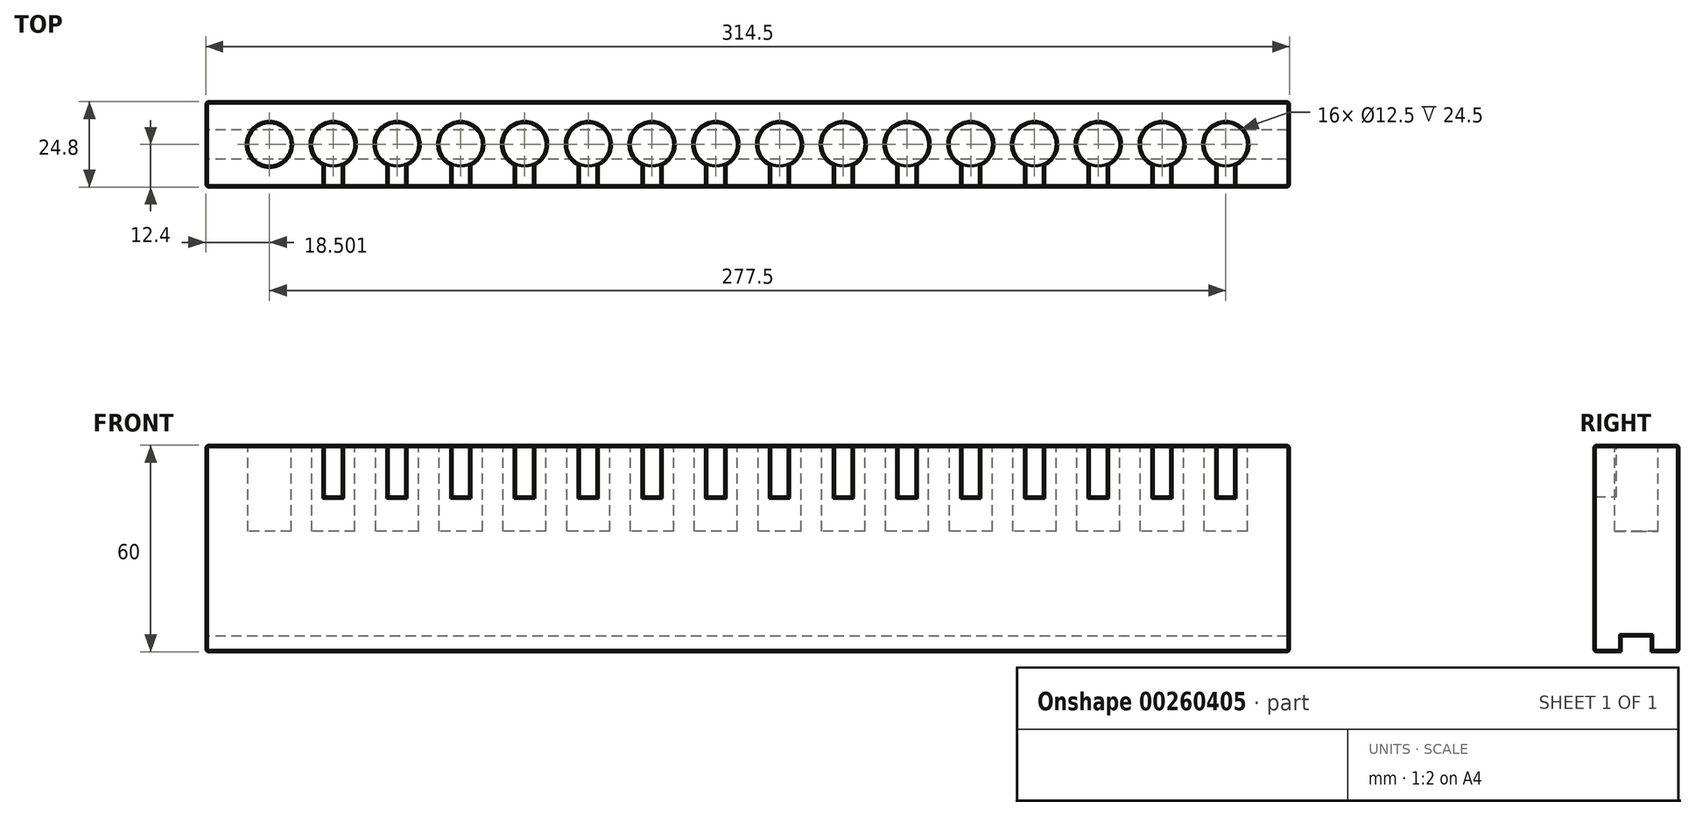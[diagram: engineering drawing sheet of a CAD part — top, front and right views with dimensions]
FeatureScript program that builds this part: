
annotation { "Feature Type Name" : "Feature", "Feature Type Description" : "" }
export const myFeature = defineFeature(function(context is Context, id is Id, definition is map)
    precondition{}
    {
        {
            var Q0;
            Q0=qCreatedBy(makeId("Front.planeOp"),FACE);
            var sketch = newSketch(context, id + "F0", { "sketchPlane" : qUnion([Q0])});
            skLineSegment(sketch, "E0.bottom", {"start": v(-141.6, 0) * mm, "end": v(172.9, 0) * mm});
            skLineSegment(sketch, "E0.top", {"start": v(-141.6, 60) * mm, "end": v(172.9, 60) * mm});
            skLineSegment(sketch, "E0.left", {"start": v(-141.6, 0) * mm, "end": v(-141.6, 60) * mm});
            skLineSegment(sketch, "E0.right", {"start": v(172.9, 0) * mm, "end": v(172.9, 60) * mm});
            skLineSegment(sketch, "E1.bottom", {"start": v(-125.6, 60) * mm, "end": v(-120.6, 60) * mm});
            skLineSegment(sketch, "E1.top", {"start": v(-125.6, 45) * mm, "end": v(-120.6, 45) * mm});
            skLineSegment(sketch, "E1.left", {"start": v(-125.6, 60) * mm, "end": v(-125.6, 45) * mm});
            skLineSegment(sketch, "E1.right", {"start": v(-120.6, 60) * mm, "end": v(-120.6, 45) * mm});
            skLineSegment(sketch, "E2.1.0.0", {"start": v(-107.1, 60) * mm, "end": v(-107.1, 45) * mm});
            skLineSegment(sketch, "E2.1.0.1", {"start": v(-107.1, 60) * mm, "end": v(-102.1, 60) * mm});
            skLineSegment(sketch, "E2.1.0.2", {"start": v(-102.1, 60) * mm, "end": v(-102.1, 45) * mm});
            skLineSegment(sketch, "E2.1.0.3", {"start": v(-107.1, 45) * mm, "end": v(-102.1, 45) * mm});
            skLineSegment(sketch, "E2.2.0.0", {"start": v(-88.6, 60) * mm, "end": v(-88.6, 45) * mm});
            skLineSegment(sketch, "E2.2.0.1", {"start": v(-88.6, 60) * mm, "end": v(-83.6, 60) * mm});
            skLineSegment(sketch, "E2.2.0.2", {"start": v(-83.6, 60) * mm, "end": v(-83.6, 45) * mm});
            skLineSegment(sketch, "E2.2.0.3", {"start": v(-88.6, 45) * mm, "end": v(-83.6, 45) * mm});
            skLineSegment(sketch, "E2.3.0.0", {"start": v(-70.1, 60) * mm, "end": v(-70.1, 45) * mm});
            skLineSegment(sketch, "E2.3.0.1", {"start": v(-70.1, 60) * mm, "end": v(-65.1, 60) * mm});
            skLineSegment(sketch, "E2.3.0.2", {"start": v(-65.1, 60) * mm, "end": v(-65.1, 45) * mm});
            skLineSegment(sketch, "E2.3.0.3", {"start": v(-70.1, 45) * mm, "end": v(-65.1, 45) * mm});
            skLineSegment(sketch, "E2.4.0.0", {"start": v(-51.6, 60) * mm, "end": v(-51.6, 45) * mm});
            skLineSegment(sketch, "E2.4.0.1", {"start": v(-51.6, 60) * mm, "end": v(-46.6, 60) * mm});
            skLineSegment(sketch, "E2.4.0.2", {"start": v(-46.6, 60) * mm, "end": v(-46.6, 45) * mm});
            skLineSegment(sketch, "E2.4.0.3", {"start": v(-51.6, 45) * mm, "end": v(-46.6, 45) * mm});
            skLineSegment(sketch, "E2.5.0.0", {"start": v(-33.1, 60) * mm, "end": v(-33.1, 45) * mm});
            skLineSegment(sketch, "E2.5.0.1", {"start": v(-33.1, 60) * mm, "end": v(-28.1, 60) * mm});
            skLineSegment(sketch, "E2.5.0.2", {"start": v(-28.1, 60) * mm, "end": v(-28.1, 45) * mm});
            skLineSegment(sketch, "E2.5.0.3", {"start": v(-33.1, 45) * mm, "end": v(-28.1, 45) * mm});
            skLineSegment(sketch, "E2.6.0.0", {"start": v(-14.6, 60) * mm, "end": v(-14.6, 45) * mm});
            skLineSegment(sketch, "E2.6.0.1", {"start": v(-14.6, 60) * mm, "end": v(-9.6, 60) * mm});
            skLineSegment(sketch, "E2.6.0.2", {"start": v(-9.6, 60) * mm, "end": v(-9.6, 45) * mm});
            skLineSegment(sketch, "E2.6.0.3", {"start": v(-14.6, 45) * mm, "end": v(-9.6, 45) * mm});
            skLineSegment(sketch, "E2.7.0.0", {"start": v(3.9, 60) * mm, "end": v(3.9, 45) * mm});
            skLineSegment(sketch, "E2.7.0.1", {"start": v(3.9, 60) * mm, "end": v(8.9, 60) * mm});
            skLineSegment(sketch, "E2.7.0.2", {"start": v(8.9, 60) * mm, "end": v(8.9, 45) * mm});
            skLineSegment(sketch, "E2.7.0.3", {"start": v(3.9, 45) * mm, "end": v(8.9, 45) * mm});
            skLineSegment(sketch, "E2.8.0.0", {"start": v(22.4, 60) * mm, "end": v(22.4, 45) * mm});
            skLineSegment(sketch, "E2.8.0.1", {"start": v(22.4, 60) * mm, "end": v(27.4, 60) * mm});
            skLineSegment(sketch, "E2.8.0.2", {"start": v(27.4, 60) * mm, "end": v(27.4, 45) * mm});
            skLineSegment(sketch, "E2.8.0.3", {"start": v(22.4, 45) * mm, "end": v(27.4, 45) * mm});
            skLineSegment(sketch, "E2.9.0.0", {"start": v(40.9, 60) * mm, "end": v(40.9, 45) * mm});
            skLineSegment(sketch, "E2.9.0.1", {"start": v(40.9, 60) * mm, "end": v(45.9, 60) * mm});
            skLineSegment(sketch, "E2.9.0.2", {"start": v(45.9, 60) * mm, "end": v(45.9, 45) * mm});
            skLineSegment(sketch, "E2.9.0.3", {"start": v(40.9, 45) * mm, "end": v(45.9, 45) * mm});
            skLineSegment(sketch, "E2.10.0.0", {"start": v(59.4, 60) * mm, "end": v(59.4, 45) * mm});
            skLineSegment(sketch, "E2.10.0.1", {"start": v(59.4, 60) * mm, "end": v(64.4, 60) * mm});
            skLineSegment(sketch, "E2.10.0.2", {"start": v(64.4, 60) * mm, "end": v(64.4, 45) * mm});
            skLineSegment(sketch, "E2.10.0.3", {"start": v(59.4, 45) * mm, "end": v(64.4, 45) * mm});
            skLineSegment(sketch, "E2.11.0.0", {"start": v(77.9, 60) * mm, "end": v(77.9, 45) * mm});
            skLineSegment(sketch, "E2.11.0.1", {"start": v(77.9, 60) * mm, "end": v(82.9, 60) * mm});
            skLineSegment(sketch, "E2.11.0.2", {"start": v(82.9, 60) * mm, "end": v(82.9, 45) * mm});
            skLineSegment(sketch, "E2.11.0.3", {"start": v(77.9, 45) * mm, "end": v(82.9, 45) * mm});
            skLineSegment(sketch, "E2.12.0.0", {"start": v(96.4, 60) * mm, "end": v(96.4, 45) * mm});
            skLineSegment(sketch, "E2.12.0.1", {"start": v(96.4, 60) * mm, "end": v(101.4, 60) * mm});
            skLineSegment(sketch, "E2.12.0.2", {"start": v(101.4, 60) * mm, "end": v(101.4, 45) * mm});
            skLineSegment(sketch, "E2.12.0.3", {"start": v(96.4, 45) * mm, "end": v(101.4, 45) * mm});
            skLineSegment(sketch, "E2.13.0.0", {"start": v(114.9, 60) * mm, "end": v(114.9, 45) * mm});
            skLineSegment(sketch, "E2.13.0.1", {"start": v(114.9, 60) * mm, "end": v(119.9, 60) * mm});
            skLineSegment(sketch, "E2.13.0.2", {"start": v(119.9, 60) * mm, "end": v(119.9, 45) * mm});
            skLineSegment(sketch, "E2.13.0.3", {"start": v(114.9, 45) * mm, "end": v(119.9, 45) * mm});
            skLineSegment(sketch, "E2.14.0.0", {"start": v(133.4, 60) * mm, "end": v(133.4, 45) * mm});
            skLineSegment(sketch, "E2.14.0.1", {"start": v(133.4, 60) * mm, "end": v(138.4, 60) * mm});
            skLineSegment(sketch, "E2.14.0.2", {"start": v(138.4, 60) * mm, "end": v(138.4, 45) * mm});
            skLineSegment(sketch, "E2.14.0.3", {"start": v(133.4, 45) * mm, "end": v(138.4, 45) * mm});
            skLineSegment(sketch, "E2.15.0.0", {"start": v(151.9, 60) * mm, "end": v(151.9, 45) * mm});
            skLineSegment(sketch, "E2.15.0.1", {"start": v(151.9, 60) * mm, "end": v(156.9, 60) * mm});
            skLineSegment(sketch, "E2.15.0.2", {"start": v(156.9, 60) * mm, "end": v(156.9, 45) * mm});
            skLineSegment(sketch, "E2.15.0.3", {"start": v(151.9, 45) * mm, "end": v(156.9, 45) * mm});
            skLineSegment(sketch, "E2.direction1", {"start": v(-125.6, 45) * mm, "end": v(-107.1, 45) * mm, "construction": true});
            skLineSegment(sketch, "E3", {"start": v(-123.1, 65.93) * mm, "end": v(-123.1, 35.93) * mm, "construction": true});
            skLineSegment(sketch, "E4", {"start": v(-104.6, 65.18) * mm, "end": v(-104.6, 35.46) * mm, "construction": true});
            skPoint(sketch, "E4.endSnap0", {"position": v(-104.6, 60) * mm});
            skSolve(sketch);
        }
        {
            var Q0;
            Q0 = qSketchRegion(id + "F0", true);
            extrude(context, id + "F1", {"entities" : qUnion([Q0]), "depth" : 24.8 * mm});
        }
        {
            var Q0;
            Q0=makeQuery(id+"F1.opExtrude","SWEPT_FACE",FACE,{"disambiguationData":[OSD([sQuery(id+"F0.wireOp",EDGE,"E0.left")])]});
            var sketch = newSketch(context, id + "F2", { "sketchPlane" : qUnion([Q0])});
            skLineSegment(sketch, "E5.bottom", {"start": v(8.15, 0) * mm, "end": v(16.75, 0) * mm});
            skLineSegment(sketch, "E5.top", {"start": v(8.15, 4.5) * mm, "end": v(16.75, 4.5) * mm});
            skLineSegment(sketch, "E5.left", {"start": v(8.15, 0) * mm, "end": v(8.15, 4.5) * mm});
            skLineSegment(sketch, "E5.right", {"start": v(16.75, 0) * mm, "end": v(16.75, 4.5) * mm});
            skLineSegment(sketch, "E6", {"start": v(12.4, -27.93) * mm, "end": v(12.4, 69.4) * mm, "construction": true});
            skSolve(sketch);
        }
        {
            var Q0;
            Q0 = qSketchRegion(id + "F2", true);
            extrude(context, id + "F3", {"entities" : qUnion([Q0]), "operationType" : NewBodyOperationType.REMOVE, "oppositeDirection" : true, "depth" : 314.5 * mm});
        }
        {
            var Q0;
            Q0=makeQuery(id+"F1.opExtrude","SWEPT_FACE",FACE,{"disambiguationData":[OSD([sQuery(id+"F0.wireOp",EDGE,"E0.top")])]});
            var sketch = newSketch(context, id + "F4", { "sketchPlane" : qUnion([Q0])});
            skLineSegment(sketch, "E7", {"start": v(168.94, -12.4) * mm, "end": v(-179.3, -12.4) * mm, "construction": true});
            skCircle(sketch, "E8", {"center": v(154.4, -12.4) * mm, "radius": 6.25 * mm});
            skCircle(sketch, "E9.1.0.0", {"center": v(135.9, -12.4) * mm, "radius": 6.25 * mm});
            skCircle(sketch, "E9.2.0.0", {"center": v(117.4, -12.4) * mm, "radius": 6.25 * mm});
            skLineSegment(sketch, "E9.direction1", {"start": v(154.4, -12.4) * mm, "end": v(135.9, -12.4) * mm, "construction": true});
            skCircle(sketch, "E10.0.3.0", {"center": v(98.9, -12.4) * mm, "radius": 6.25 * mm});
            skCircle(sketch, "E10.0.4.0", {"center": v(80.4, -12.4) * mm, "radius": 6.25 * mm});
            skCircle(sketch, "E10.0.5.0", {"center": v(61.9, -12.4) * mm, "radius": 6.25 * mm});
            skCircle(sketch, "E10.0.6.0", {"center": v(43.4, -12.4) * mm, "radius": 6.25 * mm});
            skCircle(sketch, "E10.0.7.0", {"center": v(24.9, -12.4) * mm, "radius": 6.25 * mm});
            skCircle(sketch, "E10.0.8.0", {"center": v(6.4, -12.4) * mm, "radius": 6.25 * mm});
            skCircle(sketch, "E10.0.9.0", {"center": v(-12.1, -12.4) * mm, "radius": 6.25 * mm});
            skCircle(sketch, "E10.0.10.0", {"center": v(-30.6, -12.4) * mm, "radius": 6.25 * mm});
            skCircle(sketch, "E10.0.11.0", {"center": v(-49.1, -12.4) * mm, "radius": 6.25 * mm});
            skCircle(sketch, "E10.0.12.0", {"center": v(-67.6, -12.4) * mm, "radius": 6.25 * mm});
            skCircle(sketch, "E10.0.13.0", {"center": v(-86.1, -12.4) * mm, "radius": 6.25 * mm});
            skCircle(sketch, "E10.0.14.0", {"center": v(-104.6, -12.4) * mm, "radius": 6.25 * mm});
            skCircle(sketch, "E10.0.15.0", {"center": v(-123.1, -12.4) * mm, "radius": 6.25 * mm});
            skSolve(sketch);
        }
        {
            var Q0;
            Q0 = qSketchRegion(id + "F4", true);
            var Q1;
            Q1=makeQuery(id+"F4.imprint","IMPRINT",FACE,{"disambiguationData":[TD([[makeQuery(id+"F4.imprint","IMPRINT",EDGE,{"derivedFrom":sQuery(id+"F4.wireOp",EDGE,"E8")}),1.0]])]});
            extrude(context, id + "F5", {"entities" : qUnion([Q0, Q1]), "operationType" : NewBodyOperationType.REMOVE, "oppositeDirection" : true, "depth" : 25 * mm});
        }
        {
            var Q0;
            Q0=makeQuery(id+"F0.imprint","IMPRINT",FACE,{"disambiguationData":[TD([[makeQuery(id+"F0.imprint","IMPRINT",EDGE,{"derivedFrom":sQuery(id+"F0.wireOp",EDGE,"E1.bottom")}),-1.0]])]});
            var Q1;
            Q1=makeQuery(id+"F0.imprint","IMPRINT",FACE,{"disambiguationData":[TD([[makeQuery(id+"F0.imprint","IMPRINT",EDGE,{"derivedFrom":sQuery(id+"F0.wireOp",EDGE,"E2.7.0.0")}),1.0]])]});
            var Q2;
            Q2=makeQuery(id+"F0.imprint","IMPRINT",FACE,{"disambiguationData":[TD([[makeQuery(id+"F0.imprint","IMPRINT",EDGE,{"derivedFrom":sQuery(id+"F0.wireOp",EDGE,"E2.8.0.0")}),1.0]])]});
            var Q3;
            Q3=makeQuery(id+"F0.imprint","IMPRINT",FACE,{"disambiguationData":[TD([[makeQuery(id+"F0.imprint","IMPRINT",EDGE,{"derivedFrom":sQuery(id+"F0.wireOp",EDGE,"E2.4.0.0")}),1.0]])]});
            var Q4;
            Q4=makeQuery(id+"F0.imprint","IMPRINT",FACE,{"disambiguationData":[TD([[makeQuery(id+"F0.imprint","IMPRINT",EDGE,{"derivedFrom":sQuery(id+"F0.wireOp",EDGE,"E2.6.0.0")}),1.0]])]});
            var Q5;
            Q5=makeQuery(id+"F0.imprint","IMPRINT",FACE,{"disambiguationData":[TD([[makeQuery(id+"F0.imprint","IMPRINT",EDGE,{"derivedFrom":sQuery(id+"F0.wireOp",EDGE,"E2.3.0.0")}),1.0]])]});
            var Q6;
            Q6=makeQuery(id+"F0.imprint","IMPRINT",FACE,{"disambiguationData":[TD([[makeQuery(id+"F0.imprint","IMPRINT",EDGE,{"derivedFrom":sQuery(id+"F0.wireOp",EDGE,"E2.2.0.0")}),1.0]])]});
            var Q7;
            Q7=makeQuery(id+"F0.imprint","IMPRINT",FACE,{"disambiguationData":[TD([[makeQuery(id+"F0.imprint","IMPRINT",EDGE,{"derivedFrom":sQuery(id+"F0.wireOp",EDGE,"E2.1.0.0")}),1.0]])]});
            var Q8;
            Q8=makeQuery(id+"F0.imprint","IMPRINT",FACE,{"disambiguationData":[TD([[makeQuery(id+"F0.imprint","IMPRINT",EDGE,{"derivedFrom":sQuery(id+"F0.wireOp",EDGE,"E2.5.0.0")}),1.0]])]});
            var Q9;
            Q9=makeQuery(id+"F0.imprint","IMPRINT",FACE,{"disambiguationData":[TD([[makeQuery(id+"F0.imprint","IMPRINT",EDGE,{"derivedFrom":sQuery(id+"F0.wireOp",EDGE,"E2.15.0.0")}),1.0]])]});
            var Q10;
            Q10=makeQuery(id+"F0.imprint","IMPRINT",FACE,{"disambiguationData":[TD([[makeQuery(id+"F0.imprint","IMPRINT",EDGE,{"derivedFrom":sQuery(id+"F0.wireOp",EDGE,"E2.14.0.0")}),1.0]])]});
            var Q11;
            Q11=makeQuery(id+"F0.imprint","IMPRINT",FACE,{"disambiguationData":[TD([[makeQuery(id+"F0.imprint","IMPRINT",EDGE,{"derivedFrom":sQuery(id+"F0.wireOp",EDGE,"E2.9.0.0")}),1.0]])]});
            var Q12;
            Q12=makeQuery(id+"F0.imprint","IMPRINT",FACE,{"disambiguationData":[TD([[makeQuery(id+"F0.imprint","IMPRINT",EDGE,{"derivedFrom":sQuery(id+"F0.wireOp",EDGE,"E2.12.0.0")}),1.0]])]});
            var Q13;
            Q13=makeQuery(id+"F0.imprint","IMPRINT",FACE,{"disambiguationData":[TD([[makeQuery(id+"F0.imprint","IMPRINT",EDGE,{"derivedFrom":sQuery(id+"F0.wireOp",EDGE,"E2.13.0.0")}),1.0]])]});
            var Q14;
            Q14=makeQuery(id+"F0.imprint","IMPRINT",FACE,{"disambiguationData":[TD([[makeQuery(id+"F0.imprint","IMPRINT",EDGE,{"derivedFrom":sQuery(id+"F0.wireOp",EDGE,"E2.10.0.0")}),1.0]])]});
            var Q15;
            Q15=makeQuery(id+"F0.imprint","IMPRINT",FACE,{"disambiguationData":[TD([[makeQuery(id+"F0.imprint","IMPRINT",EDGE,{"derivedFrom":sQuery(id+"F0.wireOp",EDGE,"E2.11.0.0")}),1.0]])]});
            extrude(context, id + "F6", {"entities" : qUnion([Q0, Q1, Q2, Q3, Q4, Q5, Q6, Q7, Q8, Q9, Q10, Q11, Q12, Q13, Q14, Q15]), "operationType" : NewBodyOperationType.REMOVE, "depth" : 25 * mm, "hasSecondDirection" : true, "secondDirectionOppositeDirection" : false, "secondDirectionDepth" : 12 * mm});
        }
        {
            var Q0;
            Q0=makeQuery(id+"F1.opExtrude","SWEPT_FACE",FACE,{"disambiguationData":[OSD([sQuery(id+"F0.wireOp",EDGE,"E0.top")])]});
            var Q1;
            Q1=makeQuery(id+"F1.opExtrude","CAP_FACE",FACE,{"disambiguationData":[OSD([sQuery(id+"F0.wireOp",EDGE,"E0.bottom"),sQuery(id+"F0.wireOp",EDGE,"E0.top"),sQuery(id+"F0.wireOp",EDGE,"E0.left"),sQuery(id+"F0.wireOp",EDGE,"E0.right")])],"isStart":false});
            var Q2;
            Q2=makeQuery(id+"F1.opExtrude","SWEPT_FACE",FACE,{"disambiguationData":[OSD([sQuery(id+"F0.wireOp",EDGE,"E0.left")])]});
            var Q3;
            Q3=makeQuery(id+"F1.opExtrude","CAP_FACE",FACE,{"disambiguationData":[OSD([sQuery(id+"F0.wireOp",EDGE,"E0.bottom"),sQuery(id+"F0.wireOp",EDGE,"E0.top"),sQuery(id+"F0.wireOp",EDGE,"E0.left"),sQuery(id+"F0.wireOp",EDGE,"E0.right")])],"isStart":true});
            var Q4;
            Q4=makeQuery(id+"F1.opExtrude","SWEPT_FACE",FACE,{"disambiguationData":[OSD([sQuery(id+"F0.wireOp",EDGE,"E0.right")])]});
            chamfer(context, id + "F7", {"entities" : qUnion([Q0, Q1, Q2, Q3, Q4]), "width" : 0.5 * mm, "tangentPropagation" : true});
        }
    });
